SOLIDWORKS PART (.sldprt)
format: sldprt  version: not decoded by parser v0  size: 222,208 bytes
history: native  units: mm
features: plane x4, sketch x3, extrude x3, material x1, dome x1, shell x1 (+8 scaffold rows collapsed)
feature tree (21):
  scaffold x8  (default folders/planes/origin — collapsed)
  material  "Matériau <non spécifié>"
  plane  "Plan de face"
  plane  "Plan de dessus"
  plane  "Plan de droite"
  sketch  "Esquisse1"
  extrude  "Boss.-Extru.1"  Depth=1mm
  dome  "Dôme1"
  shell  "Coque1"  Thickness=2mm
  plane  "Plan1"
  sketch  "Esquisse3"  dims[c1.D5=2.6mm c1.D1=31.0mm c1.D2=31.0mm c1.D3=6.0mm c1.D4=~8.611941mm c2.D4=90.0deg c3.D4=8.0mm c3.D6=~13.632885mm c4.D4=6.8175mm c4.D7=~6.815385mm]
  extrude  "Boss.-Extru.2"  [1 undecoded]
  sketch  "Esquisse4"  dims[D1=2.05mm D2=2.05mm D3=2.05mm D4=2.05mm D5=1.0mm D6=1.0mm D7=1.0mm D8=1.0mm]
  extrude  "Boss.-Extru.3"  Depth=5mm
decode coverage: 5 of 8 modeling features carry decoded parameters
note: ~ marks probable driven/reference dimensions
note: 1 parameter value undecoded
note: suppression state not decoded; provenance and decode notes live in map.json
